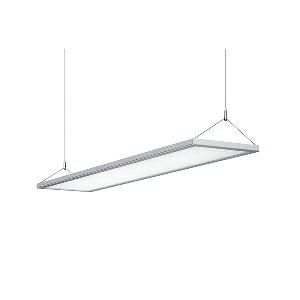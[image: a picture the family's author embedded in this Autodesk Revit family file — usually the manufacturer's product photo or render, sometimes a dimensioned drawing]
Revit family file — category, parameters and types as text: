
# Revit family: idoo_pendant_-_ipp_7000_vtl_d_00688763_485b
name_source: partatom
category: Lighting Fixtures
units: mm (PartAtom-declared; Revit-internal decimal feet)

## family parameters
Cut with Voids When Loaded = No
Host = Face
Light Source = No
Part Type = Normal
Room Calculation Point = No
Round Connector Dimension = Use Diameter
Shared = No

## types (1)
- IDOO.pendant - IPP 7000/VTL/D (1 x LED, 8400 lm, 2700-6500K)
    Apparent Load = 65 VA
    Approval mark = CE
    CIE Flux Codes = 55 85 96 33 100
    Color Rendering = 80-89
    Color Temperature = 2700-6500K
    Control Gear = Electronic ballast
    Default Elevation = 1800 mm
    Description = IPP 7000/VTL/D|Suspended luminaire|light source: LED Cold white 2700-6500 K  Energy efficiency category A/A+/A++|connected load: 220-240 V, 50/60 Hz|Power consumption: approx. 65 W|standby: approx. 0,50|luminous flux: 8400 lm|luminous efficacy: 129 lm/W|light distribution: Direct/indirect|direct ratio: approx. 33 %|color rendering index (CRI): >= 80|chromaticity tolerance:  3 SDCM|System of protection: IP 20|technology: Continuously dimmable|luminaire body|material: |colour: White|lamp cover: Acrylic (PMMA), Clear|mains lead: 1.00 m With free stranded wires|Fastening: Steel cable 0.3 - 0.7 m|glare control: Prism aperture|luminance(L65): <= 2800 cd/m|unified glare rating(4H 8H): <=  16|special features: Specified values when used with NET module, Direct light component with edge light and light-guide technology for homogenous light exit, Indirect light component with Batwing diffuser for wide-beam light exit, LED system: DALI Load 1 (2700 K, 49 W, 6100 lm) , DALI Load 2 (6500 K, 49 W, 6500 lm)|Approval mark: VDE - ENEC|
    Height = 30 mm  [stored 0.0984252 ft]
    Lamp = 1 x LED
    Lamp Light Flux = 8400 lm
    Lamp count = 1
    Length = 1200 mm
    Luminous efficacy = 129 lm/W
    Manufacturer = Waldmann
    ModVariant = No
    Model = 00688763
    Mounting Place = Ceiling
    Mounting Type = Pendant
    Number of Poles = 1
    OnlyDefault = Yes
    Power Factor = 1
    Product Name = IDOO.pendant - IPP 7000/VTL/D
    Product group = Suspended luminaire
    ProductGroupID = 9
    Protection Class = Protection class I
    Protection Degree = IP 20
    RLX_Detail_Level = 1
    RLX_Emergency_Light_Flux = 0 lm
    RLX_Emergency_Type = 0
    RLX_Emergency_Type_DB = No
    RlxData = <blob elided: 32677 chars, md5=b982f195>
    Socket = socket
    Standby Power = 0 W
    System Light Flux = 8400 lm
    System Power = 65 W
    Type Comments = Product without accessories
    Type Image = 113263000-00688760.jpg
    URL = http://relux.com
    VarID = ---
    Voltage = 230 V
    Voltage Range = 220-240 V
    Weight = 0.00 kg
    Width = 250 mm

note: [stored X ft] marks values corroborated as IEEE doubles in the binary element streams (Revit-internal decimal feet)

## geometry (parser evidence)
native form markers: Blend x4, Sweep x11
no freeform markers — native parametric forms only
